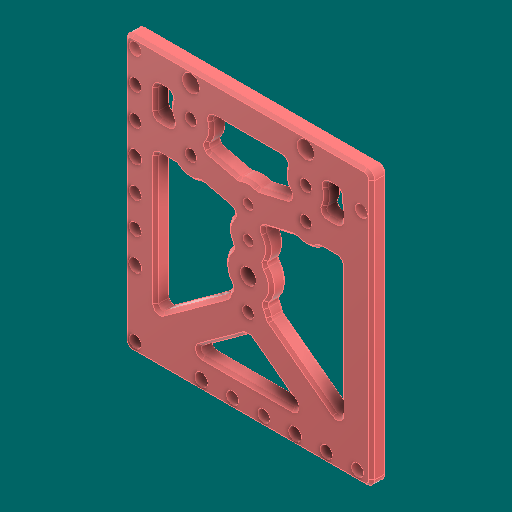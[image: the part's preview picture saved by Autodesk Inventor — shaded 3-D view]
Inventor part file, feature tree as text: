
AUTODESK INVENTOR PART (.ipt)
format: ipt  version: 2023.1 (Build 271208000, 208)  size: 544,768 bytes
history: native  units: in
note: dims shown in document units (in); Inventor stores cm internally (conversion verified against a paired STEP export)
features: other x3, sketch x2
ambient origin geometry x8: Origin, YZ Plane, XZ Plane, XY Plane, X Axis, Y Axis, Z Axis, Center Point
bodies: Solid1 (feature_tree)
feature tree (5):
  other  "TopPlate.ipt"
  other  "Solid1::TopPlate.ipt"
  other  "TaggingFeature1"
  sketch  "Sketch1"  dims[d0=0.3937in]
  sketch  "Sketch2"
